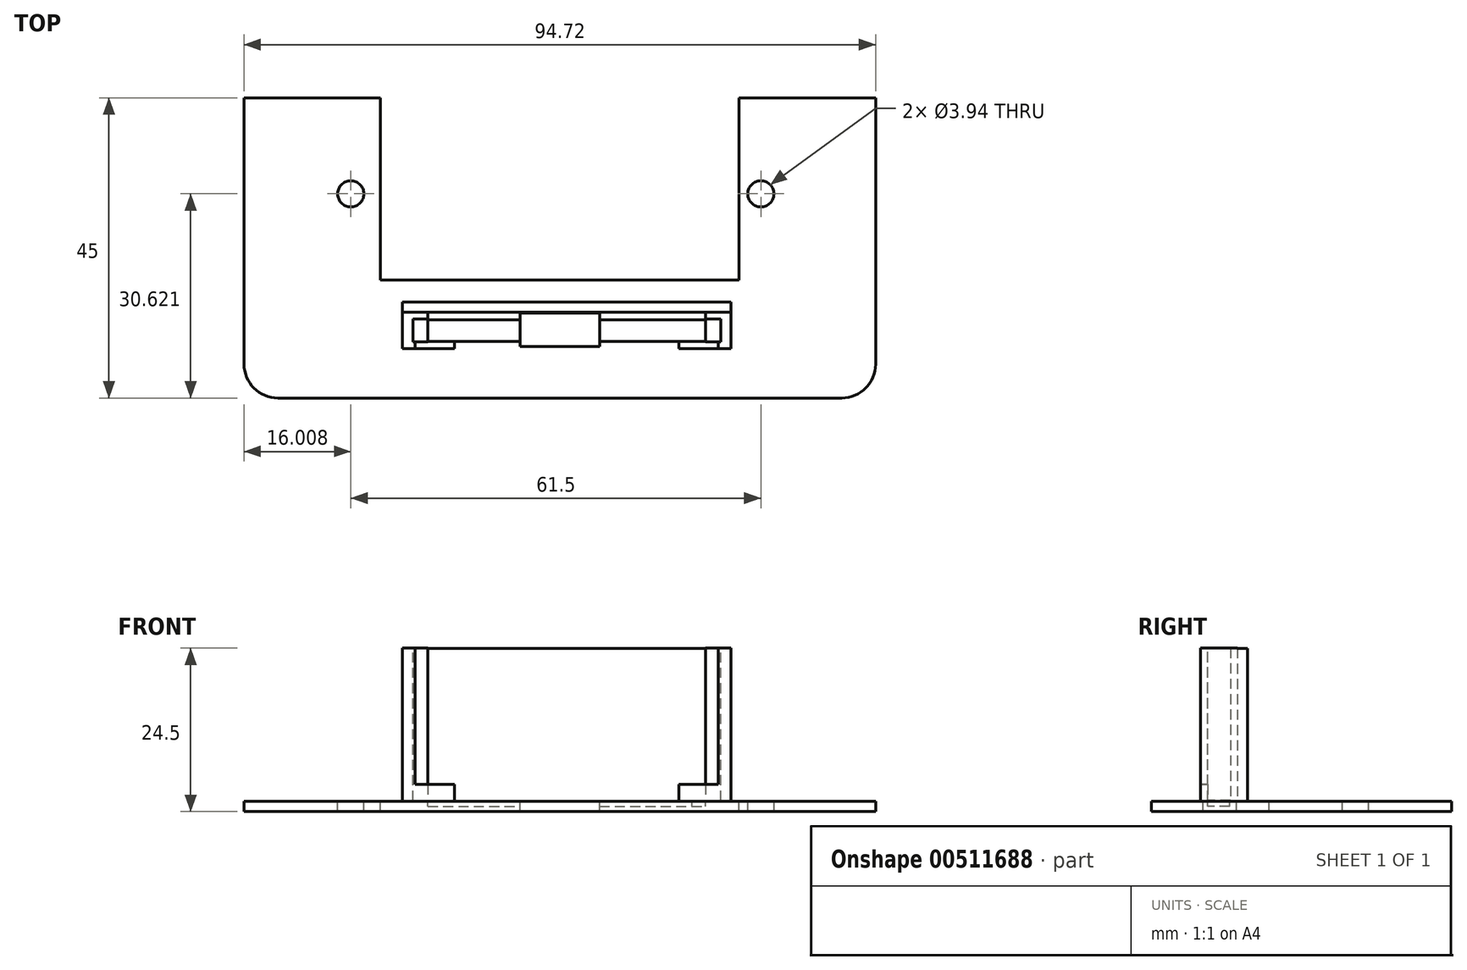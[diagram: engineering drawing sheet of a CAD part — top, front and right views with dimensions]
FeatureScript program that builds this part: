
annotation { "Feature Type Name" : "Feature", "Feature Type Description" : "" }
export const myFeature = defineFeature(function(context is Context, id is Id, definition is map)
    precondition{}
    {
        {
            var Q0;
            Q0=qCreatedBy(makeId("Top.planeOp"),FACE);
            var sketch = newSketch(context, id + "F0", { "sketchPlane" : qUnion([Q0])});
            skLineSegment(sketch, "E0.bottom", {"start": v(-47.36, 22.5) * mm, "end": v(47.36, 22.5) * mm});
            skLineSegment(sketch, "E0.top", {"start": v(-47.36, -22.5) * mm, "end": v(47.36, -22.5) * mm});
            skLineSegment(sketch, "E0.left", {"start": v(-47.36, 22.5) * mm, "end": v(-47.36, -22.5) * mm});
            skLineSegment(sketch, "E0.right", {"start": v(47.36, 22.5) * mm, "end": v(47.36, -22.5) * mm});
            skPoint(sketch, "E0.middle", {"position": v(0, 0) * mm});
            skSolve(sketch);
        }
        {
            var Q0;
            Q0 = qSketchRegion(id + "F0", true);
            extrude(context, id + "F1", {"entities" : qUnion([Q0]), "depth" : 1.5 * mm});
        }
        {
            var Q0;
            Q0=makeQuery(id+"F1.opExtrude","CAP_FACE",FACE,{"disambiguationData":[OSD([sQuery(id+"F0.wireOp",EDGE,"E0.bottom"),sQuery(id+"F0.wireOp",EDGE,"E0.top"),sQuery(id+"F0.wireOp",EDGE,"E0.left"),sQuery(id+"F0.wireOp",EDGE,"E0.right")])],"isStart":false});
            var sketch = newSketch(context, id + "F2", { "sketchPlane" : qUnion([Q0])});
            skLineSegment(sketch, "E1", {"start": v(-31.35, 8.12) * mm, "end": v(30.15, 8.12) * mm});
            skSolve(sketch);
        }
        {
            var Q0;
            Q0=sQuery(id+"F2.wireOp",VERTEX,"E1.start");
            var Q1;
            Q1=makeQuery(id+"F1.opExtrude","SWEPT_BODY",BODY,{"disambiguationData":[OSD([sQuery(id+"F0.wireOp",EDGE,"E0.bottom"),sQuery(id+"F0.wireOp",EDGE,"E0.top"),sQuery(id+"F0.wireOp",EDGE,"E0.left"),sQuery(id+"F0.wireOp",EDGE,"E0.right")])]});
            hole(context, id + "F3", {"style" : HoleStyle.SIMPLE, "endStyle" : HoleEndStyle.BLIND, "holeDiameter" : 3.94 * mm, "holeDepth" : 25.4 * mm, "isTappedThrough" : true, "tappedDepth" : 12.7 * mm, "tapClearance" : 3, "locations" : qUnion([Q0]), "scope" : qUnion([Q1])});
        }
        {
            var Q0;
            Q0=sQuery(id+"F2.wireOp",VERTEX,"E1.end");
            var Q1;
            Q1=makeQuery(id+"F1.opExtrude","SWEPT_BODY",BODY,{"disambiguationData":[OSD([sQuery(id+"F0.wireOp",EDGE,"E0.bottom"),sQuery(id+"F0.wireOp",EDGE,"E0.top"),sQuery(id+"F0.wireOp",EDGE,"E0.left"),sQuery(id+"F0.wireOp",EDGE,"E0.right")])]});
            hole(context, id + "F4", {"style" : HoleStyle.SIMPLE, "endStyle" : HoleEndStyle.BLIND, "holeDiameter" : 3.94 * mm, "holeDepth" : 25.4 * mm, "isTappedThrough" : true, "tappedDepth" : 12.7 * mm, "tapClearance" : 3, "locations" : qUnion([Q0]), "scope" : qUnion([Q1])});
        }
        {
            var Q0;
            Q0=makeQuery(id+"F1.opExtrude","CAP_FACE",FACE,{"disambiguationData":[OSD([sQuery(id+"F0.wireOp",EDGE,"E0.bottom"),sQuery(id+"F0.wireOp",EDGE,"E0.top"),sQuery(id+"F0.wireOp",EDGE,"E0.left"),sQuery(id+"F0.wireOp",EDGE,"E0.right")])],"isStart":false});
            var sketch = newSketch(context, id + "F5", { "sketchPlane" : qUnion([Q0])});
            skLineSegment(sketch, "E2.bottom", {"start": v(-25, 22.5) * mm, "end": v(25, 22.5) * mm});
            skLineSegment(sketch, "E2.top", {"start": v(-25, 9.76) * mm, "end": v(25, 9.76) * mm});
            skLineSegment(sketch, "E2.left", {"start": v(-25, 22.5) * mm, "end": v(-25, 9.76) * mm});
            skLineSegment(sketch, "E2.right", {"start": v(25, 22.5) * mm, "end": v(25, 9.76) * mm});
            skPoint(sketch, "E2.middle", {"position": v(0, 16.13) * mm});
            skSolve(sketch);
        }
        {
            var Q0;
            Q0 = qSketchRegion(id + "F5", true);
            extrude(context, id + "F6", {"entities" : qUnion([Q0]), "operationType" : NewBodyOperationType.REMOVE, "oppositeDirection" : true, "depth" : 25.4 * mm});
        }
        {
            var Q0;
            Q0=makeQuery(id+"F1.opExtrude","SWEPT_EDGE",EDGE,{"disambiguationData":[OSD([sQuery(id+"F0.wireOp",EDGE,"E0.top"),sQuery(id+"F0.wireOp",EDGE,"E0.left")])]});
            var Q1;
            Q1=makeQuery(id+"F1.opExtrude","SWEPT_EDGE",EDGE,{"disambiguationData":[OSD([sQuery(id+"F0.wireOp",EDGE,"E0.top"),sQuery(id+"F0.wireOp",EDGE,"E0.right")])]});
            fillet(context, id + "F7", {"entities" : qUnion([Q0, Q1]), "radius" : 5.08 * mm, "tangentPropagation" : true, "allowEdgeOverflow" : false});
        }
        {
            var Q0;
            Q0=makeQuery(id+"F1.opExtrude","CAP_FACE",FACE,{"disambiguationData":[OSD([sQuery(id+"F0.wireOp",EDGE,"E0.bottom"),sQuery(id+"F0.wireOp",EDGE,"E0.top"),sQuery(id+"F0.wireOp",EDGE,"E0.left"),sQuery(id+"F0.wireOp",EDGE,"E0.right")])],"isStart":false});
            var sketch = newSketch(context, id + "F8", { "sketchPlane" : qUnion([Q0])});
            skLineSegment(sketch, "E3.bottom", {"start": v(-25, 10.42) * mm, "end": v(25, 10.42) * mm});
            skLineSegment(sketch, "E3.top", {"start": v(-25, -4.82) * mm, "end": v(25, -4.82) * mm});
            skLineSegment(sketch, "E3.left", {"start": v(-25, 10.42) * mm, "end": v(-25, -4.82) * mm});
            skLineSegment(sketch, "E3.right", {"start": v(25, 10.42) * mm, "end": v(25, -4.82) * mm});
            skPoint(sketch, "E3.middle", {"position": v(0, 2.8) * mm});
            skPoint(sketch, "E3.middle.positionSnap0", {"position": v(0, 9.76) * mm});
            skPoint(sketch, "E3.centerSnap0", {"position": v(0, 9.76) * mm});
            skSolve(sketch);
        }
        {
            var Q0;
            Q0 = qSketchRegion(id + "F8", true);
            extrude(context, id + "F9", {"entities" : qUnion([Q0]), "operationType" : NewBodyOperationType.REMOVE, "oppositeDirection" : true, "depth" : 25.4 * mm});
        }
        {
            var Q0;
            Q0=makeQuery(id+"F1.opExtrude","CAP_FACE",FACE,{"disambiguationData":[OSD([sQuery(id+"F0.wireOp",EDGE,"E0.bottom"),sQuery(id+"F0.wireOp",EDGE,"E0.top"),sQuery(id+"F0.wireOp",EDGE,"E0.left"),sQuery(id+"F0.wireOp",EDGE,"E0.right")])],"isStart":false});
            var sketch = newSketch(context, id + "F10", { "sketchPlane" : qUnion([Q0])});
            skLineSegment(sketch, "E4.bottom", {"start": v(-5.95, -9.75) * mm, "end": v(5.95, -9.75) * mm});
            skLineSegment(sketch, "E4.top", {"start": v(-5.95, -14.75) * mm, "end": v(5.95, -14.75) * mm});
            skLineSegment(sketch, "E4.left", {"start": v(-5.95, -9.75) * mm, "end": v(-5.95, -14.75) * mm});
            skLineSegment(sketch, "E4.right", {"start": v(5.95, -9.75) * mm, "end": v(5.95, -14.75) * mm});
            skPoint(sketch, "E4.middle", {"position": v(0, -12.25) * mm});
            skSolve(sketch);
        }
        {
            var Q0;
            Q0 = qSketchRegion(id + "F10", true);
            extrude(context, id + "F11", {"entities" : qUnion([Q0]), "operationType" : NewBodyOperationType.REMOVE, "oppositeDirection" : true, "depth" : 25.4 * mm});
        }
        {
            var Q0;
            Q0=makeQuery(id+"F1.opExtrude","CAP_FACE",FACE,{"disambiguationData":[OSD([sQuery(id+"F0.wireOp",EDGE,"E0.bottom"),sQuery(id+"F0.wireOp",EDGE,"E0.top"),sQuery(id+"F0.wireOp",EDGE,"E0.left"),sQuery(id+"F0.wireOp",EDGE,"E0.right")])],"isStart":false});
            var sketch = newSketch(context, id + "F12", { "sketchPlane" : qUnion([Q0])});
            skPoint(sketch, "E5", {"position": v(-21.7, -12.36) * mm});
            skPoint(sketch, "E6", {"position": v(23.75, -12.36) * mm});
            skLineSegment(sketch, "E7.bottom", {"start": v(-23.6, -9.6) * mm, "end": v(-19.8, -9.6) * mm});
            skLineSegment(sketch, "E7.top", {"start": v(-23.6, -15.1) * mm, "end": v(-19.8, -15.1) * mm});
            skLineSegment(sketch, "E7.left", {"start": v(-23.6, -9.6) * mm, "end": v(-23.6, -15.1) * mm});
            skLineSegment(sketch, "E7.right", {"start": v(-19.8, -9.6) * mm, "end": v(-19.8, -15.1) * mm});
            skLineSegment(sketch, "E8.bottom", {"start": v(21.85, -9.6) * mm, "end": v(25.66, -9.6) * mm});
            skLineSegment(sketch, "E8.top", {"start": v(21.85, -15.1) * mm, "end": v(25.66, -15.1) * mm});
            skLineSegment(sketch, "E8.left", {"start": v(21.85, -9.6) * mm, "end": v(21.85, -15.1) * mm});
            skLineSegment(sketch, "E8.right", {"start": v(25.66, -9.6) * mm, "end": v(25.66, -15.1) * mm});
            skPoint(sketch, "E9", {"position": v(0, -12.25) * mm});
            skPoint(sketch, "E9.positionSnap0", {"position": v(-5.95, -12.25) * mm});
            skSolve(sketch);
        }
        {
            var Q0;
            Q0 = qSketchRegion(id + "F12", true);
            extrude(context, id + "F13", {"entities" : qUnion([Q0]), "operationType" : NewBodyOperationType.ADD, "depth" : 23 * mm});
        }
        {
            var Q0;
            Q0=makeQuery(id+"F13.opExtrude","CAP_FACE",FACE,{"disambiguationData":[OSD([sQuery(id+"F12.wireOp",EDGE,"E7.bottom"),sQuery(id+"F12.wireOp",EDGE,"E7.top"),sQuery(id+"F12.wireOp",EDGE,"E7.left"),sQuery(id+"F12.wireOp",EDGE,"E7.right")])],"isStart":false});
            var sketch = newSketch(context, id + "F14", { "sketchPlane" : qUnion([Q0])});
            skLineSegment(sketch, "E10.bottom", {"start": v(-22.05, -10.65) * mm, "end": v(-17.53, -10.65) * mm});
            skLineSegment(sketch, "E10.top", {"start": v(-22.05, -14.07) * mm, "end": v(-17.53, -14.07) * mm});
            skLineSegment(sketch, "E10.left", {"start": v(-22.05, -10.65) * mm, "end": v(-22.05, -14.07) * mm});
            skLineSegment(sketch, "E10.right", {"start": v(-17.53, -10.65) * mm, "end": v(-17.53, -14.07) * mm});
            skPoint(sketch, "E10.middle", {"position": v(-19.8, -12.36) * mm});
            skSolve(sketch);
        }
        {
            var Q0;
            Q0 = qSketchRegion(id + "F14", true);
            extrude(context, id + "F15", {"entities" : qUnion([Q0]), "operationType" : NewBodyOperationType.REMOVE, "oppositeDirection" : true, "depth" : 22.86 * mm});
        }
        {
            var Q0;
            Q0=makeQuery(id+"F13.opExtrude","CAP_FACE",FACE,{"disambiguationData":[OSD([sQuery(id+"F12.wireOp",EDGE,"E8.bottom"),sQuery(id+"F12.wireOp",EDGE,"E8.top"),sQuery(id+"F12.wireOp",EDGE,"E8.left"),sQuery(id+"F12.wireOp",EDGE,"E8.right")])],"isStart":false});
            var sketch = newSketch(context, id + "F16", { "sketchPlane" : qUnion([Q0])});
            skLineSegment(sketch, "E11.bottom", {"start": v(19.59, -10.64) * mm, "end": v(24.11, -10.64) * mm});
            skLineSegment(sketch, "E11.top", {"start": v(19.59, -14.07) * mm, "end": v(24.11, -14.07) * mm});
            skLineSegment(sketch, "E11.left", {"start": v(19.59, -10.64) * mm, "end": v(19.59, -14.07) * mm});
            skLineSegment(sketch, "E11.right", {"start": v(24.11, -10.64) * mm, "end": v(24.11, -14.07) * mm});
            skPoint(sketch, "E11.middle", {"position": v(21.85, -12.36) * mm});
            skSolve(sketch);
        }
        {
            var Q0;
            Q0 = qSketchRegion(id + "F16", true);
            extrude(context, id + "F17", {"entities" : qUnion([Q0]), "operationType" : NewBodyOperationType.REMOVE, "oppositeDirection" : true, "depth" : 22.86 * mm});
        }
        {
            var Q0;
            Q0=makeQuery(id+"F1.opExtrude","CAP_FACE",FACE,{"disambiguationData":[OSD([sQuery(id+"F0.wireOp",EDGE,"E0.bottom"),sQuery(id+"F0.wireOp",EDGE,"E0.top"),sQuery(id+"F0.wireOp",EDGE,"E0.left"),sQuery(id+"F0.wireOp",EDGE,"E0.right")])],"isStart":false});
            var sketch = newSketch(context, id + "F18", { "sketchPlane" : qUnion([Q0])});
            skLineSegment(sketch, "E12.bottom", {"start": v(-19.8, -14.04) * mm, "end": v(19.8, -14.04) * mm});
            skLineSegment(sketch, "E12.top", {"start": v(-19.8, -10.75) * mm, "end": v(19.8, -10.75) * mm});
            skLineSegment(sketch, "E12.left", {"start": v(-19.8, -14.04) * mm, "end": v(-19.8, -10.75) * mm});
            skLineSegment(sketch, "E12.right", {"start": v(19.8, -14.04) * mm, "end": v(19.8, -10.75) * mm});
            skPoint(sketch, "E12.middle", {"position": v(0, -12.4) * mm});
            skPoint(sketch, "E12.middle.positionSnap0", {"position": v(0, -14.75) * mm});
            skPoint(sketch, "E12.centerSnap0", {"position": v(0, -14.75) * mm});
            skLineSegment(sketch, "E13.bottom", {"start": v(19.8, -10.75) * mm, "end": v(21.85, -10.75) * mm});
            skLineSegment(sketch, "E13.top", {"start": v(19.8, -14.04) * mm, "end": v(21.85, -14.04) * mm});
            skLineSegment(sketch, "E13.left", {"start": v(19.8, -10.75) * mm, "end": v(19.8, -14.04) * mm});
            skLineSegment(sketch, "E13.right", {"start": v(21.85, -10.75) * mm, "end": v(21.85, -14.04) * mm});
            skSolve(sketch);
        }
        {
            var Q0;
            Q0 = qSketchRegion(id + "F18", true);
            extrude(context, id + "F19", {"entities" : qUnion([Q0]), "operationType" : NewBodyOperationType.REMOVE, "oppositeDirection" : true, "depth" : 0.76 * mm});
        }
        {
            var Q0;
            Q0=makeQuery(id+"F1.opExtrude","CAP_FACE",FACE,{"disambiguationData":[OSD([sQuery(id+"F0.wireOp",EDGE,"E0.bottom"),sQuery(id+"F0.wireOp",EDGE,"E0.top"),sQuery(id+"F0.wireOp",EDGE,"E0.left"),sQuery(id+"F0.wireOp",EDGE,"E0.right")])],"isStart":false});
            var sketch = newSketch(context, id + "F20", { "sketchPlane" : qUnion([Q0])});
            skLineSegment(sketch, "E14.bottom", {"start": v(-23.6, -9.6) * mm, "end": v(25.66, -9.6) * mm});
            skLineSegment(sketch, "E14.top", {"start": v(-23.6, -8.1) * mm, "end": v(25.66, -8.1) * mm});
            skLineSegment(sketch, "E14.left", {"start": v(-23.6, -9.6) * mm, "end": v(-23.6, -8.1) * mm});
            skLineSegment(sketch, "E14.right", {"start": v(25.66, -9.6) * mm, "end": v(25.66, -8.1) * mm});
            skSolve(sketch);
        }
        {
            var Q0;
            Q0 = qSketchRegion(id + "F20", true);
            extrude(context, id + "F21", {"entities" : qUnion([Q0]), "operationType" : NewBodyOperationType.ADD, "depth" : 22.96 * mm});
        }
        {
            var Q0;
            {var subQ0=sQuery(id+"F0.wireOp",EDGE,"E0.right");var subQ9=sQuery(id+"F0.wireOp",EDGE,"E0.left");var subQ10=sQuery(id+"F0.wireOp",EDGE,"E0.top");var subQ11=sQuery(id+"F0.wireOp",EDGE,"E0.bottom");var subQ12=makeQuery(id+"F1.opExtrude","CAP_FACE",FACE,{"disambiguationData":[OSD([subQ11,subQ10,subQ9,subQ0])],"isStart":false});Q0=makeQuery(id+"F21.boolean.opBoolean","SPLIT",FACE,{"disambiguationData":[TD([makeQuery(id+"F1.opExtrude","SWEPT_FACE",FACE,{"disambiguationData":[OSD([subQ11])]})])],"derivedFrom":subQ12});}
            var sketch = newSketch(context, id + "F22", { "sketchPlane" : qUnion([Q0])});
            skLineSegment(sketch, "E15.bottom", {"start": v(-19.8, -15.1) * mm, "end": v(-15.8, -15.1) * mm});
            skLineSegment(sketch, "E15.top", {"start": v(-19.8, -14.04) * mm, "end": v(-15.8, -14.04) * mm});
            skLineSegment(sketch, "E15.left", {"start": v(-19.8, -15.1) * mm, "end": v(-19.8, -14.04) * mm});
            skLineSegment(sketch, "E15.right", {"start": v(-15.8, -15.1) * mm, "end": v(-15.8, -14.04) * mm});
            skLineSegment(sketch, "E16.bottom", {"start": v(21.85, -15.1) * mm, "end": v(17.85, -15.1) * mm});
            skLineSegment(sketch, "E16.top", {"start": v(21.85, -14.04) * mm, "end": v(17.85, -14.04) * mm});
            skLineSegment(sketch, "E16.left", {"start": v(21.85, -15.1) * mm, "end": v(21.85, -14.04) * mm});
            skLineSegment(sketch, "E16.right", {"start": v(17.85, -15.1) * mm, "end": v(17.85, -14.04) * mm});
            skSolve(sketch);
        }
        {
            var Q0;
            Q0 = qSketchRegion(id + "F22", true);
            extrude(context, id + "F23", {"entities" : qUnion([Q0]), "operationType" : NewBodyOperationType.ADD, "depth" : 2.54 * mm});
        }
        {
            var Q0;
            {var subQ0=sQuery(id+"F0.wireOp",EDGE,"E0.right");var subQ1=sQuery(id+"F0.wireOp",EDGE,"E0.left");var subQ2=sQuery(id+"F0.wireOp",EDGE,"E0.top");var subQ3=sQuery(id+"F0.wireOp",EDGE,"E0.bottom");var subQ4=makeQuery(id+"F1.opExtrude","CAP_FACE",FACE,{"disambiguationData":[OSD([subQ3,subQ2,subQ1,subQ0])],"isStart":false});var subQ30=makeQuery(id+"F1.opExtrude","SWEPT_FACE",FACE,{"disambiguationData":[OSD([subQ3])]});Q0=makeQuery(id+"F23.boolean.opBoolean","SPLIT",FACE,{"disambiguationData":[TD([subQ30])],"derivedFrom":makeQuery(id+"F21.boolean.opBoolean","SPLIT",FACE,{"disambiguationData":[TD([subQ30])],"derivedFrom":subQ4})});}
            var sketch = newSketch(context, id + "F24", { "sketchPlane" : qUnion([Q0])});
            skLineSegment(sketch, "E17.bottom", {"start": v(-25, -4.82) * mm, "end": v(-26.9, -4.82) * mm});
            skLineSegment(sketch, "E17.top", {"start": v(-25, 22.5) * mm, "end": v(-26.9, 22.5) * mm});
            skLineSegment(sketch, "E17.left", {"start": v(-25, -4.82) * mm, "end": v(-25, 22.5) * mm});
            skLineSegment(sketch, "E17.right", {"start": v(-26.9, -4.82) * mm, "end": v(-26.9, 22.5) * mm});
            skLineSegment(sketch, "E18.bottom", {"start": v(25, -4.82) * mm, "end": v(26.9, -4.82) * mm});
            skLineSegment(sketch, "E18.top", {"start": v(25, 22.5) * mm, "end": v(26.9, 22.5) * mm});
            skLineSegment(sketch, "E18.left", {"start": v(25, -4.82) * mm, "end": v(25, 22.5) * mm});
            skLineSegment(sketch, "E18.right", {"start": v(26.9, -4.82) * mm, "end": v(26.9, 22.5) * mm});
            skSolve(sketch);
        }
        {
            var Q0;
            Q0 = qSketchRegion(id + "F24", true);
            extrude(context, id + "F25", {"entities" : qUnion([Q0]), "operationType" : NewBodyOperationType.REMOVE, "oppositeDirection" : true, "depth" : 25.4 * mm, "offsetDistance" : 25.4 * mm});
        }
        {
            var Q0;
            Q0=makeQuery(id+"F23.boolean.opBoolean","MERGE",FACE,{"derivedFrom":[makeQuery(id+"F13.opExtrude","SWEPT_FACE",FACE,{"disambiguationData":[OSD([sQuery(id+"F12.wireOp",EDGE,"E7.top")])]}),makeQuery(id+"F23.opExtrude","SWEPT_FACE",FACE,{"disambiguationData":[OSD([sQuery(id+"F22.wireOp",EDGE,"E15.bottom")])]})]});
            var sketch = newSketch(context, id + "F26", { "sketchPlane" : qUnion([Q0])});
            skLineSegment(sketch, "E19.bottom", {"start": v(-19.8, 4.04) * mm, "end": v(-21.7, 4.04) * mm});
            skLineSegment(sketch, "E19.top", {"start": v(-19.8, 24.5) * mm, "end": v(-21.7, 24.5) * mm});
            skLineSegment(sketch, "E19.left", {"start": v(-19.8, 4.04) * mm, "end": v(-19.8, 24.5) * mm});
            skLineSegment(sketch, "E19.right", {"start": v(-21.7, 4.04) * mm, "end": v(-21.7, 24.5) * mm});
            skSolve(sketch);
        }
        {
            var Q0;
            Q0 = qSketchRegion(id + "F26", true);
            extrude(context, id + "F27", {"entities" : qUnion([Q0]), "operationType" : NewBodyOperationType.REMOVE, "oppositeDirection" : true, "depth" : 1.65 * mm, "offsetDistance" : 25.4 * mm});
        }
        {
            var Q0;
            Q0=makeQuery(id+"F23.boolean.opBoolean","MERGE",FACE,{"derivedFrom":[makeQuery(id+"F13.opExtrude","SWEPT_FACE",FACE,{"disambiguationData":[OSD([sQuery(id+"F12.wireOp",EDGE,"E8.top")])]}),makeQuery(id+"F23.opExtrude","SWEPT_FACE",FACE,{"disambiguationData":[OSD([sQuery(id+"F22.wireOp",EDGE,"E16.bottom")])]})]});
            var sketch = newSketch(context, id + "F28", { "sketchPlane" : qUnion([Q0])});
            skLineSegment(sketch, "E20.bottom", {"start": v(21.85, 4.04) * mm, "end": v(23.75, 4.04) * mm});
            skLineSegment(sketch, "E20.top", {"start": v(21.85, 24.5) * mm, "end": v(23.75, 24.5) * mm});
            skLineSegment(sketch, "E20.left", {"start": v(21.85, 4.04) * mm, "end": v(21.85, 24.5) * mm});
            skLineSegment(sketch, "E20.right", {"start": v(23.75, 4.04) * mm, "end": v(23.75, 24.5) * mm});
            skSolve(sketch);
        }
        {
            var Q0;
            Q0 = qSketchRegion(id + "F28", true);
            extrude(context, id + "F29", {"entities" : qUnion([Q0]), "operationType" : NewBodyOperationType.REMOVE, "oppositeDirection" : true, "depth" : 3.05 * mm, "offsetDistance" : 25.4 * mm});
        }
    });
